# Revit family: FLX_Spotlight_Ninety-Nine_Ceiling Hosted
name_source: partatom
category: Lighting Fixtures
revit_build: Autodesk Revit 2018 (Build: 20180423_1000(x64)
units: mm (PartAtom-declared; Revit-internal decimal feet)

## family parameters
Always vertical = Yes
Cut with Voids When Loaded = No
Host = Ceiling
Light Source = Yes
OmniClass Number = 23.80.70.11
OmniClass Title = Luminaries for Internal Lighting
Part Type = Normal
Room Calculation Point = No
Round Connector Dimension = Use Diameter
Shared = No

## types (8) — shared parameters
21deg Soft Beam = No
2700K = No
3000K = No
3500K = No
38deg Soft Beam = No
4000K = No
59deg Soft Beam = No
Analogue 1-10V = No
Casambi = No
Color Filter = 16777215
DALI = No
Description = Ninety-Nine™ Spotlight
Dimming Lamp Color Temperature Shift = <None>
Emit Shape Visible in Rendering = No
Emit from Circle Diameter = 72.8 mm  [stored 0.238845 ft]
Honeycomb Louvre = No
Manufacturer = Factorylux®
Model = Please Select 01 Option For Each Configuration Category in The Family Type Properties
No Accessory = Yes
Photometric Web File = 541280473-1_phot_ninety-nine-2000lmchip-2700k-21deg_2303.ies
Spreader Lens = No
Tilt Angle = 90.00°
Type Comments = Please use the Type Catalog to get the correct photometric. This is a generic family type and the photometric representation may not correspond to your specification.
URL = https://factorylux.com
Uniclass2015Code = Pr_70_70_48_82
Uniclass2015Title = Spotlights
Uniclass2015Version = Products v1.31
Wall Wash = No

## per-type parameters (varying)
| type | Black | Control Light Source Alignment | Control Tilt Angle Center Position | Disc Monopoint | Finish | Large Monopoint | Small Monopoint | Stone Rumbled Aluminium | Support Height | Track Adapter | Type Image |
| _Generic_Disc Monopoint, Black | Yes | 192.4 mm  [stored 0.631234 ft] | 42.4 mm  [stored 0.139108 ft] | Yes | FLX_Finish_Black | No | No | No | 2 mm  [stored 0.00656168 ft] | No | 541792887-ninety-nine-2023_disc_black.jpg |
| _Generic_Disc Monopoint, Stone Rumbled Aluminium | No | 192.4 mm  [stored 0.631234 ft] | 42.4 mm  [stored 0.139108 ft] | Yes | FLX_Finish_Stone Rumbled Aluminium | No | No | Yes | 2 mm  [stored 0.00656168 ft] | No | 541792898-ninety-nine-2023_disc_stonerumbled.jpg |
| _Generic_Large Monopoint, Black | Yes | 265 mm  [stored 0.869423 ft] | 115 mm  [stored 0.377297 ft] | No | FLX_Finish_Black | Yes | No | No | 75 mm | No | 541792909-ninety-nine-2023_l-mono_black.jpg |
| _Generic_Large Monopoint, Stone Rumbled Aluminium | No | 265 mm  [stored 0.869423 ft] | 115 mm  [stored 0.377297 ft] | No | FLX_Finish_Stone Rumbled Aluminium | Yes | No | Yes | 75 mm | No | 541792917-ninety-nine-2023_l-mono_stonerumbled.jpg |
| _Generic_Small Monopoint, Stone Rumbled Aluminium | No | 220 mm  [stored 0.721785 ft] | 70 mm  [stored 0.229659 ft] | No | FLX_Finish_Stone Rumbled Aluminium | No | Yes | Yes | 30 mm  [stored 0.0984252 ft] | No | 541792879-ninety-nine-2023_s-mono_stonerumbled.jpg |
| _Generic_Small Monopoint, Black | Yes | 220 mm  [stored 0.721785 ft] | 70 mm  [stored 0.229659 ft] | No | FLX_Finish_Black | No | Yes | No | 30 mm  [stored 0.0984252 ft] | No | 541792883-ninety-nine-2023_s-mono_black.jpg |
| _Generic_Track Adapter, Black | Yes | 244.562 mm | 94.562 mm  [stored 0.310243 ft] | No | FLX_Finish_Black | No | No | No | 54.562 mm | Yes | 541792927-ninety-nine-2023_track_black.jpg |
| _Generic_Track Adapter, Stone Rumbled Aluminium | No | 244.562 mm | 94.562 mm  [stored 0.310243 ft] | No | FLX_Finish_Stone Rumbled Aluminium | No | No | Yes | 54.562 mm | Yes | 541792936-ninety-nine-2023_track_stonerumbled.jpg |

note: [stored X ft] marks values corroborated as IEEE doubles in the binary element streams (Revit-internal decimal feet)

## geometry (parser evidence)
native form markers: Sweep x5
no freeform markers — native parametric forms only
